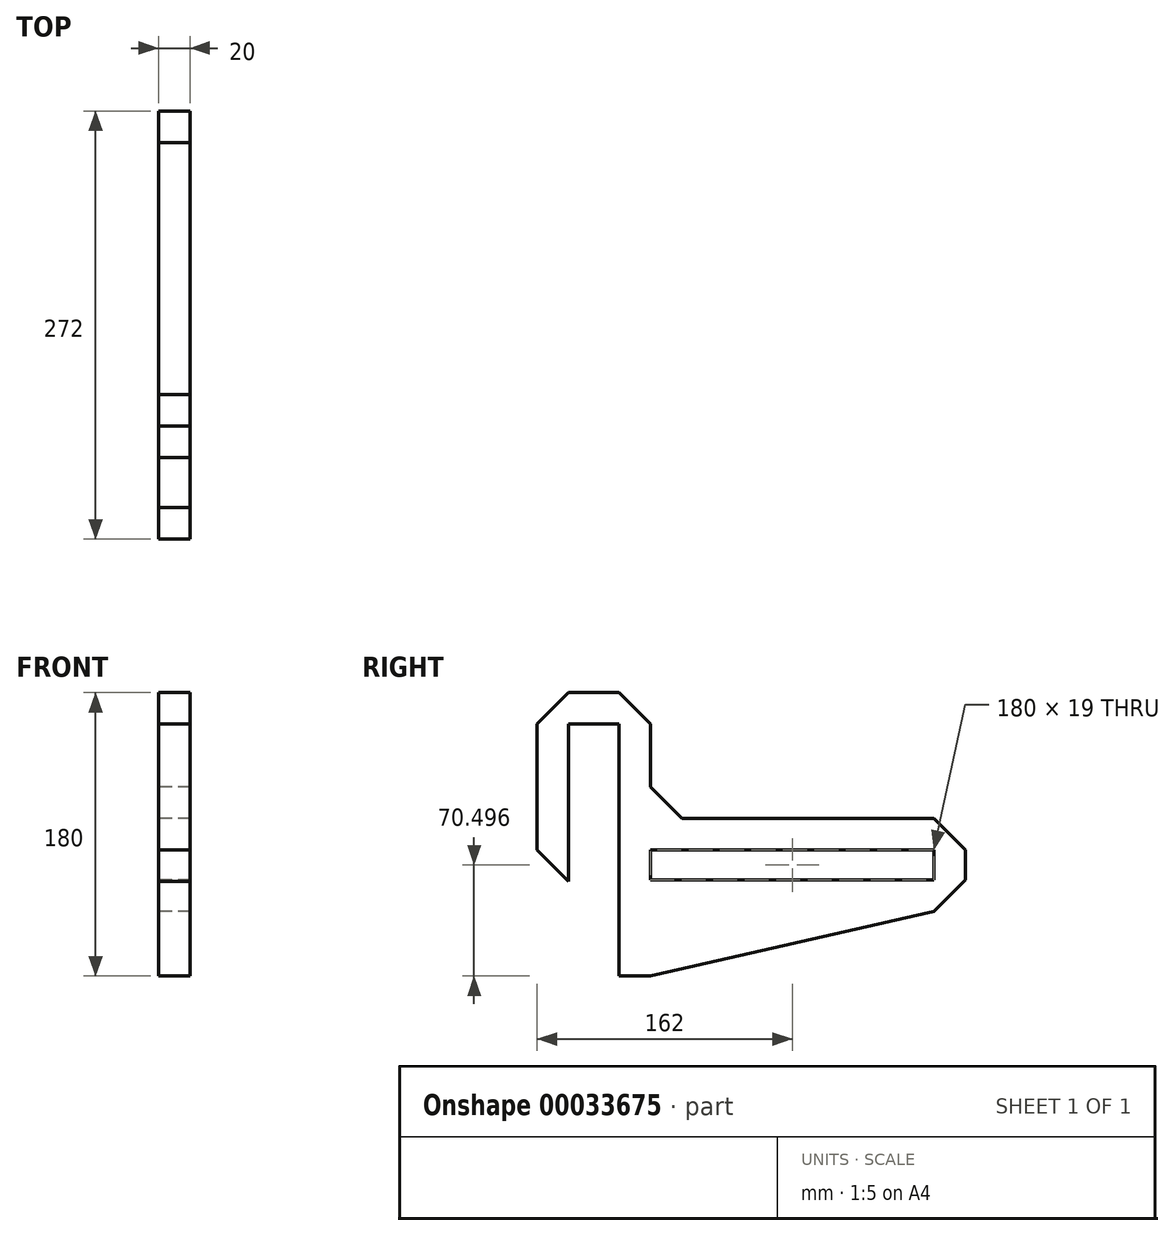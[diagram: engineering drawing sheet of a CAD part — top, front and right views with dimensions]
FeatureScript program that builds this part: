
annotation { "Feature Type Name" : "Feature", "Feature Type Description" : "" }
export const myFeature = defineFeature(function(context is Context, id is Id, definition is map)
    precondition{}
    {
        {
            var Q0;
            Q0=qCreatedBy(makeId("Right.planeOp"),FACE);
            var sketch = newSketch(context, id + "F0", { "sketchPlane" : qUnion([Q0])});
            skLineSegment(sketch, "E0", {"start": v(52, -60.8) * mm, "end": v(72, -60.8) * mm});
            skLineSegment(sketch, "E1", {"start": v(272, 0.2) * mm, "end": v(272, 19.2) * mm});
            skLineSegment(sketch, "E2", {"start": v(272, 19.2) * mm, "end": v(252, 39.2) * mm});
            skLineSegment(sketch, "E3", {"start": v(252, 39.2) * mm, "end": v(92, 39.2) * mm});
            skLineSegment(sketch, "E4", {"start": v(92, 39.2) * mm, "end": v(72, 59.2) * mm});
            skLineSegment(sketch, "E5", {"start": v(72, 59.2) * mm, "end": v(72, 99.2) * mm});
            skLineSegment(sketch, "E6", {"start": v(72, 99.2) * mm, "end": v(52, 119.2) * mm});
            skLineSegment(sketch, "E7", {"start": v(52, 119.2) * mm, "end": v(20, 119.2) * mm});
            skLineSegment(sketch, "E8", {"start": v(20, 119.2) * mm, "end": v(0, 99.2) * mm});
            skLineSegment(sketch, "E9", {"start": v(20, -0.8) * mm, "end": v(20, 99.2) * mm});
            skLineSegment(sketch, "E10", {"start": v(20, 99.2) * mm, "end": v(52, 99.2) * mm});
            skLineSegment(sketch, "E11", {"start": v(52, 99.2) * mm, "end": v(52, -60.8) * mm});
            skLineSegment(sketch, "E12.bottom", {"start": v(252, 19.2) * mm, "end": v(72, 19.2) * mm});
            skLineSegment(sketch, "E12.top", {"start": v(252, 0.2) * mm, "end": v(72, 0.2) * mm});
            skLineSegment(sketch, "E12.left", {"start": v(252, 19.2) * mm, "end": v(252, 0.2) * mm});
            skLineSegment(sketch, "E12.right", {"start": v(72, 19.2) * mm, "end": v(72, 0.2) * mm});
            skLineSegment(sketch, "E13", {"start": v(272, 0.2) * mm, "end": v(252, -19.8) * mm});
            skPoint(sketch, "E13.endSnap0", {"position": v(252, 9.7) * mm});
            skLineSegment(sketch, "E14", {"start": v(72, -60.8) * mm, "end": v(252, -19.8) * mm});
            skLineSegment(sketch, "E15", {"start": v(20, -0.8) * mm, "end": v(0, 19.2) * mm});
            skLineSegment(sketch, "E16", {"start": v(0, 19.2) * mm, "end": v(0, 99.2) * mm});
            skSolve(sketch);
        }
        {
            var Q0;
            Q0 = qSketchRegion(id + "F0", true);
            extrude(context, id + "F1", {"entities" : qUnion([Q0]), "depth" : 20 * mm});
        }
    });
